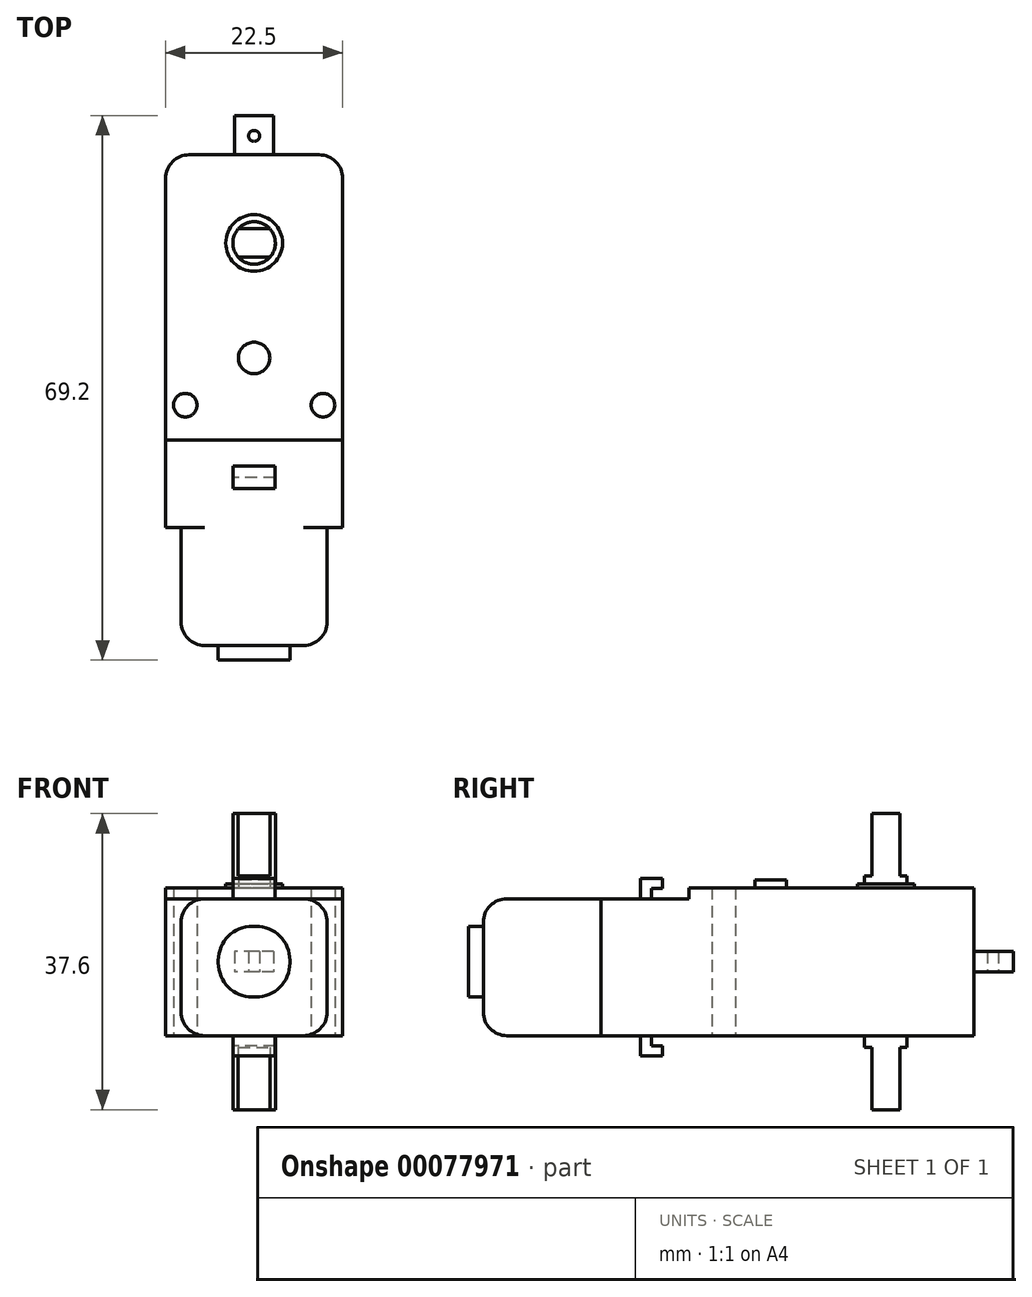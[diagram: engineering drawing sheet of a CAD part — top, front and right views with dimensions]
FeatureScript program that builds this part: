
annotation { "Feature Type Name" : "Feature", "Feature Type Description" : "" }
export const myFeature = defineFeature(function(context is Context, id is Id, definition is map)
    precondition{}
    {
        {
            var Q0;
            Q0=qCreatedBy(makeId("Top.planeOp"),FACE);
            var sketch = newSketch(context, id + "F0", { "sketchPlane" : qUnion([Q0])});
            skLineSegment(sketch, "E0", {"start": v(-11.25, -25.04) * mm, "end": v(11.25, -25.04) * mm});
            skLineSegment(sketch, "E1", {"start": v(11.25, -25.04) * mm, "end": v(11.25, 8.2) * mm});
            skLineSegment(sketch, "E2", {"start": v(8.25, 11.2) * mm, "end": v(-8.25, 11.2) * mm});
            skLineSegment(sketch, "E3", {"start": v(-11.25, 8.2) * mm, "end": v(-11.25, -25.04) * mm});
            skCircle(sketch, "E4", {"center": v(-8.75, -20.6) * mm, "radius": 1.5 * mm});
            skCircle(sketch, "E5.MirrorC", {"center": v(8.75, -20.6) * mm, "radius": 1.5 * mm});
            skLineSegment(sketch, "E6", {"start": v(-2.5, 11.2) * mm, "end": v(-2.5, 16.2) * mm});
            skLineSegment(sketch, "E7", {"start": v(-2.5, 16.2) * mm, "end": v(2.5, 16.2) * mm});
            skLineSegment(sketch, "E8", {"start": v(2.5, 16.2) * mm, "end": v(2.5, 11.2) * mm});
            skCircle(sketch, "E9", {"center": v(0, 13.6) * mm, "radius": 0.7 * mm});
            skCircle(sketch, "E10", {"center": v(0, 0) * mm, "radius": 2.7 * mm});
            skLineSegment(sketch, "E11", {"start": v(-11.25, -25.04) * mm, "end": v(-11.25, -36.17) * mm});
            skLineSegment(sketch, "E12", {"start": v(-11.25, -36.17) * mm, "end": v(11.25, -36.17) * mm});
            skLineSegment(sketch, "E13", {"start": v(11.25, -36.17) * mm, "end": v(11.25, -25.04) * mm});
            skPoint(sketch, "E14.visualSharp", {"position": v(-11.25, 11.2) * mm});
            skArc(sketch, "E14.filletArc", {"start": v(-8.25, 11.2) * mm, "mid": v(-10.37, 10.32) * mm, "end": v(-11.25, 8.2) * mm});
            skPoint(sketch, "E15.visualSharp", {"position": v(11.25, 11.2) * mm});
            skArc(sketch, "E15.filletArc", {"start": v(11.25, 8.2) * mm, "mid": v(10.37, 10.32) * mm, "end": v(8.25, 11.2) * mm});
            skLineSegment(sketch, "E16", {"start": v(-9.28, -36.17) * mm, "end": v(-9.28, -48.13) * mm});
            skLineSegment(sketch, "E17", {"start": v(-6.28, -51.13) * mm, "end": v(6.28, -51.13) * mm});
            skLineSegment(sketch, "E18", {"start": v(9.28, -48.13) * mm, "end": v(9.28, -36.17) * mm});
            skLineSegment(sketch, "E19", {"start": v(-4.55, -51.13) * mm, "end": v(-4.55, -53) * mm});
            skLineSegment(sketch, "E20", {"start": v(-4.55, -53) * mm, "end": v(4.55, -53) * mm});
            skLineSegment(sketch, "E21", {"start": v(4.55, -53) * mm, "end": v(4.55, -51.13) * mm});
            skPoint(sketch, "E22.visualSharp", {"position": v(-9.28, -51.13) * mm});
            skArc(sketch, "E22.filletArc", {"start": v(-9.28, -48.13) * mm, "mid": v(-8.4, -50.25) * mm, "end": v(-6.28, -51.13) * mm});
            skPoint(sketch, "E23.visualSharp", {"position": v(9.28, -51.13) * mm});
            skArc(sketch, "E23.filletArc", {"start": v(6.28, -51.13) * mm, "mid": v(8.4, -50.25) * mm, "end": v(9.28, -48.13) * mm});
            skLineSegment(sketch, "E24.bottom", {"start": v(-2.67, -28.35) * mm, "end": v(2.67, -28.35) * mm});
            skLineSegment(sketch, "E24.top", {"start": v(-2.67, -31.2) * mm, "end": v(2.67, -31.2) * mm});
            skLineSegment(sketch, "E24.left", {"start": v(-2.67, -28.35) * mm, "end": v(-2.67, -31.2) * mm});
            skLineSegment(sketch, "E24.right", {"start": v(2.67, -28.35) * mm, "end": v(2.67, -31.2) * mm});
            skCircle(sketch, "E25", {"center": v(0, 0) * mm, "radius": 3.6 * mm});
            skLineSegment(sketch, "E26", {"start": v(-2.01, 1.8) * mm, "end": v(2.01, 1.8) * mm});
            skLineSegment(sketch, "E27", {"start": v(-2.01, -1.8) * mm, "end": v(2.01, -1.8) * mm});
            skSolve(sketch);
        }
        {
            var Q0;
            Q0=makeQuery(id+"F0.imprint","IMPRINT",FACE,{"disambiguationData":[TD([[makeQuery(id+"F0.imprint","IMPRINT",EDGE,{"derivedFrom":sQuery(id+"F0.wireOp",EDGE,"E0")}),1.0]])]});
            var Q1;
            Q1=makeQuery(id+"F0.imprint","IMPRINT",FACE,{"disambiguationData":[TD([[makeQuery(id+"F0.imprint","IMPRINT",EDGE,{"derivedFrom":sQuery(id+"F0.wireOp",EDGE,"E25")}),1.0]])]});
            extrude(context, id + "F1", {"entities" : qUnion([Q0, Q1]), "endBound" : BoundingType.SYMMETRIC, "depth" : 18.8 * mm});
        }
        {
            var Q0;
            {var subQ1=sQuery(id+"F0.wireOp",EDGE,"E6");Q0=makeQuery(id+"F0.imprint","IMPRINT",FACE,{"disambiguationData":[TD([[makeQuery(id+"F0.imprint","IMPRINT",EDGE,{"derivedFrom":subQ1}),-1.0]])]});}
            extrude(context, id + "F2", {"entities" : qUnion([Q0]), "operationType" : NewBodyOperationType.ADD, "endBound" : BoundingType.SYMMETRIC, "depth" : 2.6 * mm});
        }
        {
            var Q0;
            Q0=makeQuery(id+"F0.imprint","IMPRINT",FACE,{"disambiguationData":[TD([[makeQuery(id+"F0.imprint","IMPRINT",EDGE,{"derivedFrom":sQuery(id+"F0.wireOp",EDGE,"E0")}),-1.0]])]});
            var Q1;
            {var subQ5=sQuery(id+"F0.wireOp",EDGE,"E16");Q1=makeQuery(id+"F0.imprint","IMPRINT",FACE,{"disambiguationData":[TD([[makeQuery(id+"F0.imprint","IMPRINT",EDGE,{"derivedFrom":subQ5}),1.0]])]});}
            extrude(context, id + "F3", {"entities" : qUnion([Q0, Q1]), "operationType" : NewBodyOperationType.ADD, "oppositeDirection" : true, "depth" : (18.8 / 2) * mm});
        }
        {
            var Q0;
            Q0=makeQuery(id+"F0.imprint","IMPRINT",FACE,{"disambiguationData":[TD([[makeQuery(id+"F0.imprint","IMPRINT",EDGE,{"derivedFrom":sQuery(id+"F0.wireOp",EDGE,"E0")}),-1.0]])]});
            var Q1;
            {var subQ5=sQuery(id+"F0.wireOp",EDGE,"E16");Q1=makeQuery(id+"F0.imprint","IMPRINT",FACE,{"disambiguationData":[TD([[makeQuery(id+"F0.imprint","IMPRINT",EDGE,{"derivedFrom":subQ5}),1.0]])]});}
            extrude(context, id + "F4", {"entities" : qUnion([Q0, Q1]), "operationType" : NewBodyOperationType.ADD, "depth" : 8 * mm});
        }
        {
            var Q0;
            {var subQ0=sQuery(id+"F0.wireOp",EDGE,"E19");Q0=makeQuery(id+"F0.imprint","IMPRINT",FACE,{"disambiguationData":[TD([[makeQuery(id+"F0.imprint","IMPRINT",EDGE,{"derivedFrom":subQ0}),1.0]])]});}
            extrude(context, id + "F5", {"entities" : qUnion([Q0]), "operationType" : NewBodyOperationType.ADD, "endBound" : BoundingType.SYMMETRIC, "depth" : 9 * mm});
        }
        {
            var Q0;
            Q0=makeQuery(id+"F3.opExtrude","CAP_EDGE",EDGE,{"disambiguationData":[OSD([sQuery(id+"F0.wireOp",EDGE,"E17")])],"isStart":false});
            var Q1;
            Q1=makeQuery(id+"F4.opExtrude","CAP_EDGE",EDGE,{"disambiguationData":[OSD([sQuery(id+"F0.wireOp",EDGE,"E17")])],"isStart":false});
            fillet(context, id + "F6", {"entities" : qUnion([Q0, Q1]), "radius" : 3 * mm, "tangentPropagation" : true, "allowEdgeOverflow" : false});
        }
        {
            var Q0;
            Q0=makeQuery(id+"F5.opExtrude","CAP_EDGE",EDGE,{"disambiguationData":[OSD([sQuery(id+"F0.wireOp",EDGE,"E21")])],"isStart":true});
            var Q1;
            Q1=makeQuery(id+"F5.opExtrude","CAP_EDGE",EDGE,{"disambiguationData":[OSD([sQuery(id+"F0.wireOp",EDGE,"E21")])],"isStart":false});
            var Q2;
            Q2=makeQuery(id+"F5.opExtrude","CAP_EDGE",EDGE,{"disambiguationData":[OSD([sQuery(id+"F0.wireOp",EDGE,"E19")])],"isStart":true});
            var Q3;
            Q3=makeQuery(id+"F5.opExtrude","CAP_EDGE",EDGE,{"disambiguationData":[OSD([sQuery(id+"F0.wireOp",EDGE,"E19")])],"isStart":false});
            fillet(context, id + "F7", {"entities" : qUnion([Q0, Q1, Q2, Q3]), "radius" : 4.33 * mm, "tangentPropagation" : true, "allowEdgeOverflow" : false});
        }
        {
            var Q0;
            {var subQ0=sQuery(id+"F0.wireOp",EDGE,"E24.left");Q0=makeQuery(id+"F4.boolean.opBoolean","MERGE",FACE,{"derivedFrom":[makeQuery(id+"F3.opExtrude","SWEPT_FACE",FACE,{"disambiguationData":[OSD([subQ0])]}),makeQuery(id+"F4.opExtrude","SWEPT_FACE",FACE,{"disambiguationData":[OSD([subQ0])]})]});}
            var sketch = newSketch(context, id + "F8", { "sketchPlane" : qUnion([Q0])});
            skLineSegment(sketch, "E28", {"start": v(-31.2, 8) * mm, "end": v(-31.2, 10.55) * mm});
            skLineSegment(sketch, "E29", {"start": v(-31.2, 10.55) * mm, "end": v(-28.35, 10.55) * mm});
            skLineSegment(sketch, "E30", {"start": v(-28.35, 10.55) * mm, "end": v(-28.35, 9.27) * mm});
            skPoint(sketch, "E30.endSnap0", {"position": v(-31.2, 9.27) * mm});
            skLineSegment(sketch, "E31", {"start": v(-28.35, 9.27) * mm, "end": v(-29.77, 9.27) * mm});
            skPoint(sketch, "E31.endSnap0", {"position": v(-29.77, 10.55) * mm});
            skLineSegment(sketch, "E32", {"start": v(-29.77, 9.27) * mm, "end": v(-29.77, 8) * mm});
            skLineSegment(sketch, "E33", {"start": v(-29.77, 8) * mm, "end": v(-28.35, 8) * mm});
            skLineSegment(sketch, "E34", {"start": v(-28.35, 8) * mm, "end": v(-28.35, -9.4) * mm});
            skLineSegment(sketch, "E35", {"start": v(-28.35, -9.4) * mm, "end": v(-29.77, -9.4) * mm});
            skLineSegment(sketch, "E36", {"start": v(-31.2, 8) * mm, "end": v(-31.2, -9.4) * mm});
            skLineSegment(sketch, "E37", {"start": v(-31.2, -9.4) * mm, "end": v(-31.2, -11.95) * mm});
            skLineSegment(sketch, "E38", {"start": v(-31.2, -11.95) * mm, "end": v(-28.35, -11.95) * mm});
            skLineSegment(sketch, "E39", {"start": v(-28.35, -11.95) * mm, "end": v(-28.35, -10.67) * mm});
            skPoint(sketch, "E39.endSnap0", {"position": v(-31.2, -10.67) * mm});
            skLineSegment(sketch, "E40", {"start": v(-28.35, -10.67) * mm, "end": v(-29.77, -10.67) * mm});
            skLineSegment(sketch, "E41", {"start": v(-29.77, -10.67) * mm, "end": v(-29.77, -9.4) * mm});
            skSolve(sketch);
        }
        {
            var Q0;
            {var subQ1=sQuery(id+"F8.wireOp",EDGE,"E28");Q0=makeQuery(id+"F8.imprint","IMPRINT",FACE,{"disambiguationData":[TD([[makeQuery(id+"F8.imprint","IMPRINT",EDGE,{"derivedFrom":subQ1}),-1.0]])]});}
            var Q1;
            {var subQ1=sQuery(id+"F8.wireOp",EDGE,"E33");Q1=makeQuery(id+"F8.imprint","IMPRINT",FACE,{"disambiguationData":[TD([[makeQuery(id+"F8.imprint","IMPRINT",EDGE,{"derivedFrom":subQ1}),1.0]])]});}
            var Q2;
            {var subQ0=sQuery(id+"F8.wireOp",EDGE,"E37");Q2=makeQuery(id+"F8.imprint","IMPRINT",FACE,{"disambiguationData":[TD([[makeQuery(id+"F8.imprint","IMPRINT",EDGE,{"derivedFrom":subQ0}),1.0]])]});}
            var Q3;
            {var subQ0=sQuery(id+"F0.wireOp",EDGE,"E24.right");Q3=makeQuery(id+"F4.boolean.opBoolean","MERGE",FACE,{"derivedFrom":[makeQuery(id+"F3.opExtrude","SWEPT_FACE",FACE,{"disambiguationData":[OSD([subQ0])]}),makeQuery(id+"F4.opExtrude","SWEPT_FACE",FACE,{"disambiguationData":[OSD([subQ0])]})]});}
            extrude(context, id + "F9", {"entities" : qUnion([Q0, Q1, Q2]), "operationType" : NewBodyOperationType.ADD, "endBound" : BoundingType.UP_TO_SURFACE, "endBoundEntityFace" : qUnion([Q3]), "depth" : 25 * mm});
        }
        {
            var Q0;
            Q0=makeQuery(id+"F1.opExtrude","CAP_FACE",FACE,{"disambiguationData":[OSD([sQuery(id+"F0.wireOp",EDGE,"E0"),sQuery(id+"F0.wireOp",EDGE,"E1"),sQuery(id+"F0.wireOp",EDGE,"E2"),sQuery(id+"F0.wireOp",EDGE,"E3"),sQuery(id+"F0.wireOp",EDGE,"E4"),sQuery(id+"F0.wireOp",EDGE,"E5.MirrorC"),sQuery(id+"F0.wireOp",EDGE,"E10"),sQuery(id+"F0.wireOp",EDGE,"E14.filletArc"),sQuery(id+"F0.wireOp",EDGE,"E15.filletArc")])],"isStart":false});
            var sketch = newSketch(context, id + "F10", { "sketchPlane" : qUnion([Q0])});
            skCircle(sketch, "E42", {"center": v(0, -14.6) * mm, "radius": 2 * mm});
            skCircle(sketch, "E43.0", {"center": v(0, 0) * mm, "radius": 3.6 * mm});
            skSolve(sketch);
        }
        {
            var Q0;
            Q0=makeQuery(id+"F10.imprint","IMPRINT",FACE,{"disambiguationData":[TD([[makeQuery(id+"F10.imprint","IMPRINT",EDGE,{"derivedFrom":sQuery(id+"F10.wireOp",EDGE,"E42")}),1.0]])]});
            extrude(context, id + "F11", {"entities" : qUnion([Q0]), "operationType" : NewBodyOperationType.ADD, "depth" : 1 * mm});
        }
        {
            var Q0;
            Q0=makeQuery(id+"F10.imprint","IMPRINT",FACE,{"disambiguationData":[TD([[makeQuery(id+"F10.imprint","IMPRINT",EDGE,{"derivedFrom":sQuery(id+"F10.wireOp",EDGE,"E43.0")}),1.0]])]});
            extrude(context, id + "F12", {"entities" : qUnion([Q0]), "operationType" : NewBodyOperationType.ADD, "depth" : 0.5 * mm});
        }
        {
            var Q0;
            {var subQ0=sQuery(id+"F0.wireOp",EDGE,"E26");Q0=makeQuery(id+"F0.imprint","IMPRINT",FACE,{"disambiguationData":[TD([[makeQuery(id+"F0.imprint","IMPRINT",EDGE,{"derivedFrom":subQ0}),-1.0]])]});}
            extrude(context, id + "F13", {"entities" : qUnion([Q0]), "endBound" : BoundingType.SYMMETRIC, "depth" : 37.6 * mm});
        }
        {
            var Q0;
            {var subQ0=sQuery(id+"F0.wireOp",EDGE,"E26");Q0=makeQuery(id+"F0.imprint","IMPRINT",FACE,{"disambiguationData":[TD([[makeQuery(id+"F0.imprint","IMPRINT",EDGE,{"derivedFrom":subQ0}),1.0]])]});}
            var Q1;
            {var subQ0=sQuery(id+"F0.wireOp",EDGE,"E27");Q1=makeQuery(id+"F0.imprint","IMPRINT",FACE,{"disambiguationData":[TD([[makeQuery(id+"F0.imprint","IMPRINT",EDGE,{"derivedFrom":subQ0}),-1.0]])]});}
            extrude(context, id + "F14", {"entities" : qUnion([Q0, Q1]), "operationType" : NewBodyOperationType.ADD, "endBound" : BoundingType.SYMMETRIC, "depth" : (37.6 - 7.9 * 2) * mm});
        }
    });
